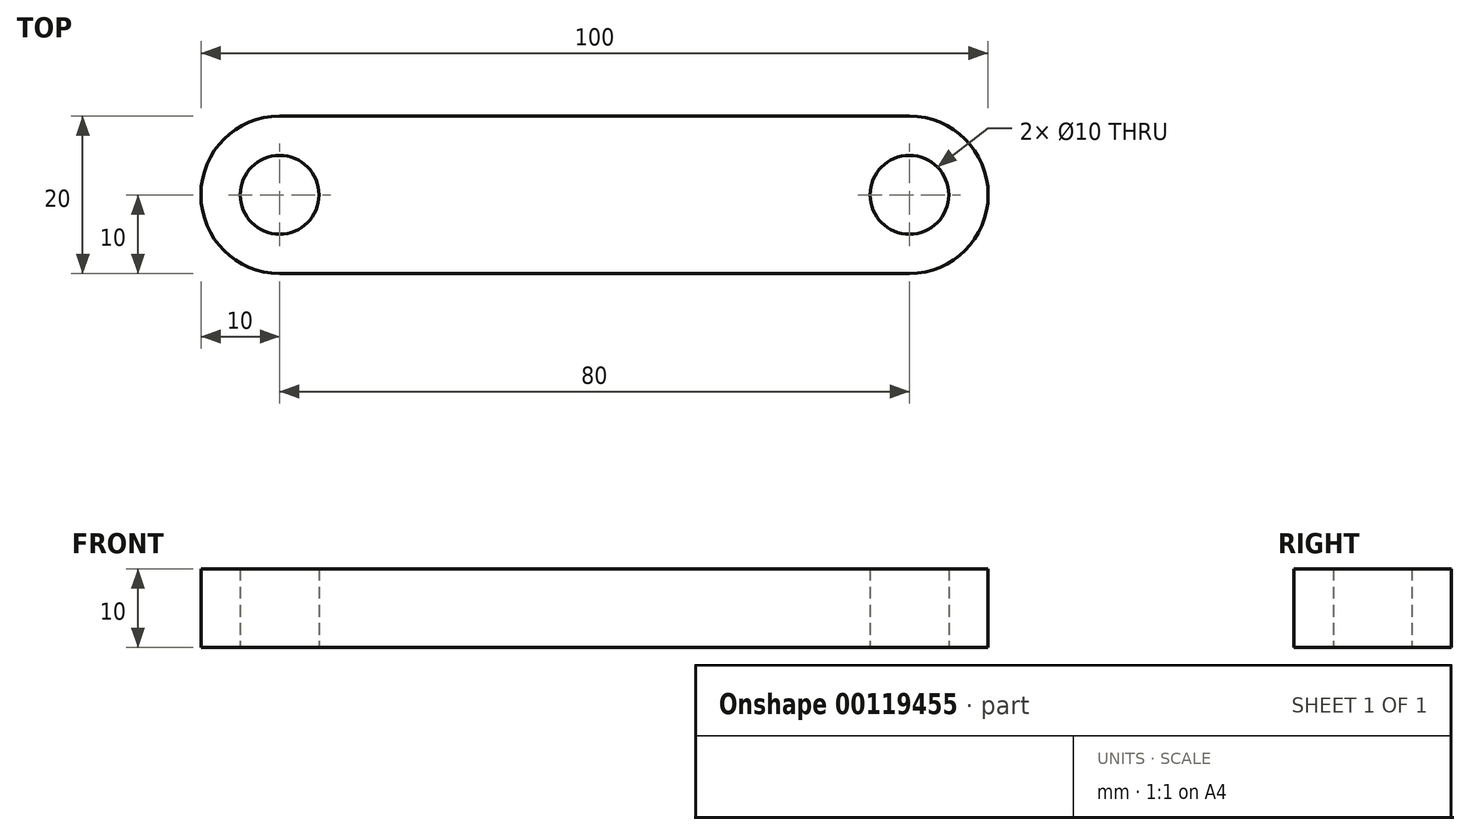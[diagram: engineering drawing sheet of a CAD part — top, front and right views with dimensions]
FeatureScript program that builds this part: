
annotation { "Feature Type Name" : "Feature", "Feature Type Description" : "" }
export const myFeature = defineFeature(function(context is Context, id is Id, definition is map)
    precondition{}
    {
        {
            var Q0;
            Q0=qCreatedBy(makeId("Top.planeOp"),FACE);
            var sketch = newSketch(context, id + "F0", { "sketchPlane" : qUnion([Q0])});
            skLineSegment(sketch, "E0.bottom", {"start": v(40, -10) * mm, "end": v(-40, -10) * mm});
            skLineSegment(sketch, "E0.top", {"start": v(40, 10) * mm, "end": v(-40, 10) * mm});
            skPoint(sketch, "E0.middle", {"position": v(0, 0) * mm});
            skCircle(sketch, "E1", {"center": v(-40, 0) * mm, "radius": 5 * mm});
            skLineSegment(sketch, "E2", {"start": v(0, 18.22) * mm, "end": v(0, -26.95) * mm, "construction": true});
            skPoint(sketch, "E2.endSnap0", {"position": v(0, -10) * mm});
            skArc(sketch, "E3", {"start": v(-40, 10) * mm, "mid": v(-50, 0) * mm, "end": v(-40, -10) * mm});
            skCircle(sketch, "E4.MirrorC", {"center": v(40, 0) * mm, "radius": 5 * mm});
            skArc(sketch, "E5.MirrorCS", {"start": v(40, 10) * mm, "mid": v(50, 0) * mm, "end": v(40, -10) * mm});
            skSolve(sketch);
        }
        {
            var Q0;
            Q0=makeQuery(id+"F0.imprint","IMPRINT",FACE,{"disambiguationData":[TD([[makeQuery(id+"F0.imprint","IMPRINT",EDGE,{"derivedFrom":sQuery(id+"F0.wireOp",EDGE,"E0.bottom")}),-1.0]])]});
            extrude(context, id + "F1", {"entities" : qUnion([Q0]), "endBound" : BoundingType.SYMMETRIC, "depth" : 10 * mm});
        }
    });
